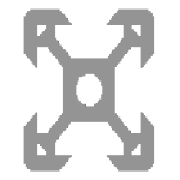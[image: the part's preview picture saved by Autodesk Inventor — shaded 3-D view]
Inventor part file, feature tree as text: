
AUTODESK INVENTOR PART (.ipt)
format: ipt  version: 2017.3 (Build 213256000, 256)  size: 196,096 bytes
history: native  units: mm
features: other x3, sketch x3, plane x1
ambient origin geometry x8: Origin, YZ Plane, XZ Plane, XY Plane, X Axis, Y Axis, Z Axis, Center Point
bodies: Solid1 (feature_tree), Body (feature_tree)
feature tree (7):
  other  "Driven Length"
  other  "Start Plane"
  other  "End Plane"
  sketch  "Sketch1"  dims[d2=4.2mm]
  sketch  "Sketch4"  dims[d3=1.5mm]
  plane  "Work Plane4"
  sketch  "Sketch5"  dims[d4=1.64mm d5=1.8mm d6=5.68mm d7=1.8mm d9=1.5mm d12=-0.0mm d13=550.0mm d14=0.13mm d15=0.0mm d18=90.0deg d17=550.0mm]
